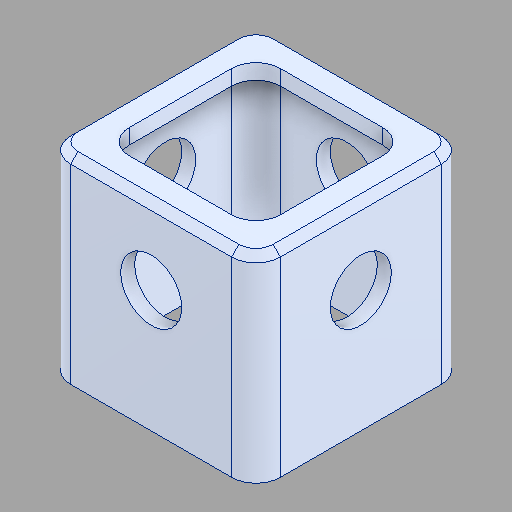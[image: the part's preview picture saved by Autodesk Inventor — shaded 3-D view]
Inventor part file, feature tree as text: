
AUTODESK INVENTOR PART (.ipt)
format: ipt  version: 2024.2 (Build 282272000, 272)  size: 151,552 bytes
history: native  units: in
note: dims shown in document units (in); Inventor stores cm internally (conversion verified against a paired STEP export)
features: chamfer x1
ambient origin geometry x8: Origin, YZ Plane, XZ Plane, XY Plane, X Axis, Y Axis, Z Axis, Center Point
bodies: Solid1 (feature_tree)
feature tree (1):
  chamfer  "Chamfer2"  [1 undecoded]
note: 1 required parameter value undecoded (feature->parameter linkage not recoverable at this tier; creation-order binding heuristic only, values carry confidence <= 0.55)
